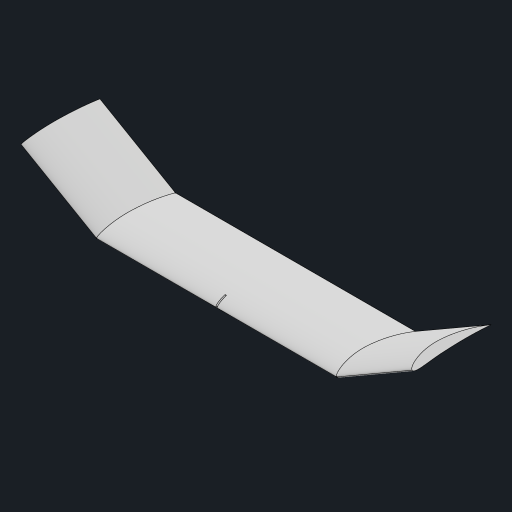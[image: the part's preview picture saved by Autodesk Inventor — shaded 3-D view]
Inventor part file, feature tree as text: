
AUTODESK INVENTOR PART (.ipt)
format: ipt  version: 2023 (Build 270158000, 158)  size: 327,680 bytes
history: native  units: mm
features: sketch x5, extrude x4, other x2, mirror x1
ambient origin geometry x8: Origin, YZ Plane, XZ Plane, XY Plane, X Axis, Y Axis, Z Axis, Center Point
bodies: Body1 (feature_tree)
feature tree (12):
  other  "ソリッド1"
  sketch  "スケッチ1"
  extrude  "押し出し1"  Depth=180.0mm TaperAngle=0.0deg
  extrude  "押し出し2"  Depth=250.0mm TaperAngle=0.0deg
  sketch  "スケッチ5"
  other  "作業平面2"
  extrude  "押し出し3"  [1 undecoded]
  mirror  "ミラー1"
  extrude  "押し出し5"  Depth=180.0mm
  sketch  "スケッチ2"
  sketch  "スケッチ6"
  sketch  "スケッチ8"
note: 1 required parameter value undecoded (feature->parameter linkage not recoverable at this tier; creation-order binding heuristic only, values carry confidence <= 0.55)
